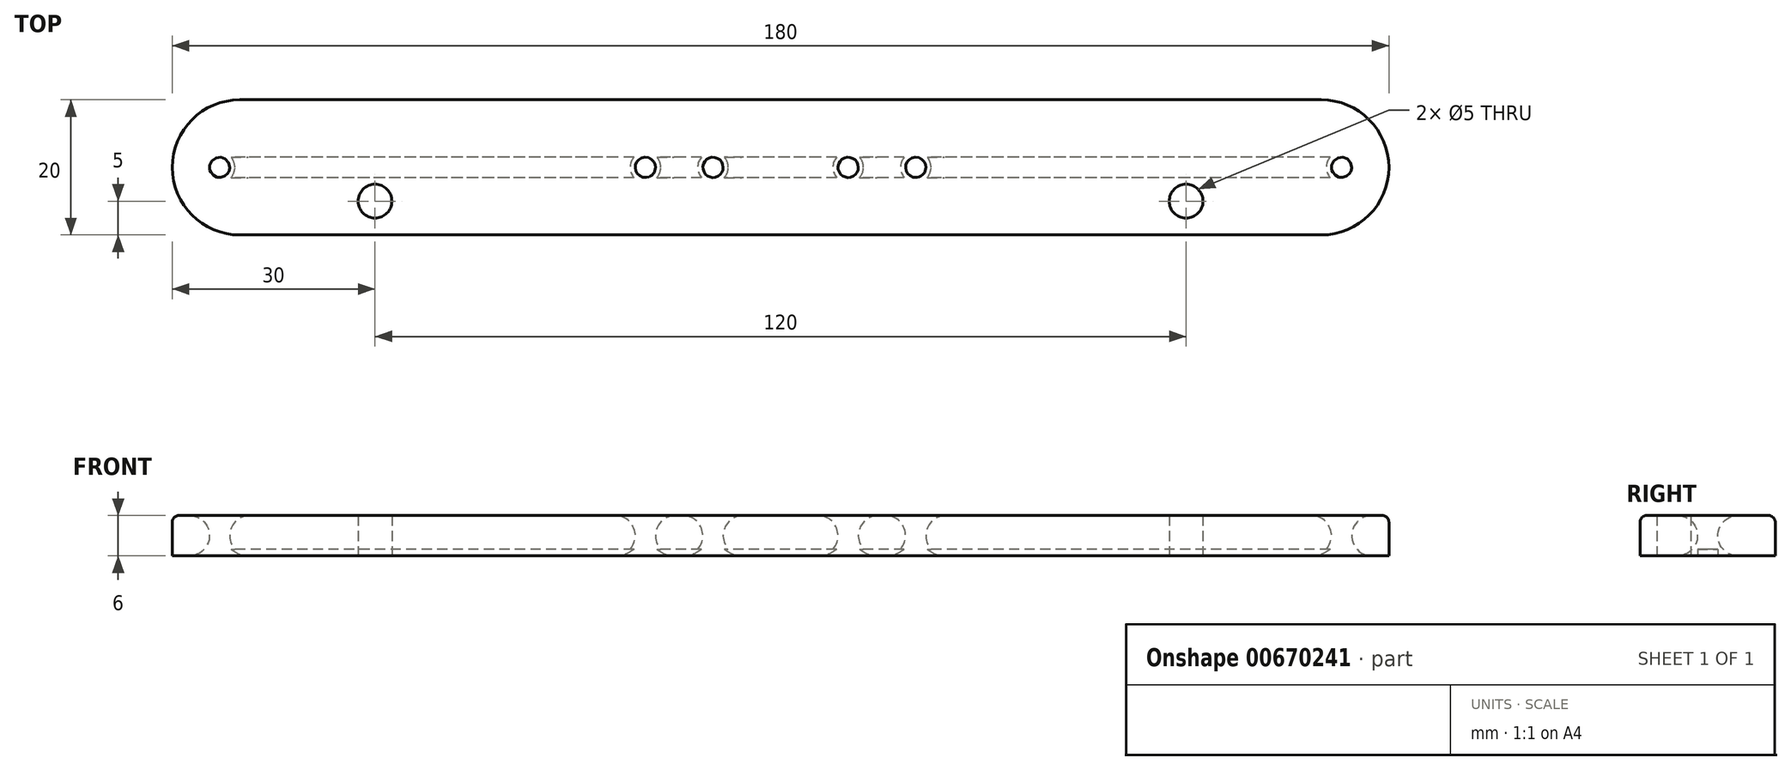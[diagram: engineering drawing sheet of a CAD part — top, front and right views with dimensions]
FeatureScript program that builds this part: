
annotation { "Feature Type Name" : "Feature", "Feature Type Description" : "" }
export const myFeature = defineFeature(function(context is Context, id is Id, definition is map)
    precondition{}
    {
        {
            var Q0;
            Q0=qCreatedBy(makeId("Top.planeOp"),FACE);
            var sketch = newSketch(context, id + "F0", { "sketchPlane" : qUnion([Q0])});
            skLineSegment(sketch, "E0.bottom", {"start": v(90, 10) * mm, "end": v(-90, 10) * mm});
            skLineSegment(sketch, "E0.top", {"start": v(90, -10) * mm, "end": v(-90, -10) * mm});
            skLineSegment(sketch, "E0.left", {"start": v(90, 10) * mm, "end": v(90, -10) * mm});
            skLineSegment(sketch, "E0.right", {"start": v(-90, 10) * mm, "end": v(-90, -10) * mm});
            skPoint(sketch, "E0.middle", {"position": v(0, 0) * mm});
            skCircle(sketch, "E1", {"center": v(-83, 0) * mm, "radius": 1.5 * mm});
            skCircle(sketch, "E2", {"center": v(-10, 0) * mm, "radius": 1.5 * mm});
            skCircle(sketch, "E3", {"center": v(-20, 0) * mm, "radius": 1.5 * mm});
            skCircle(sketch, "E4", {"center": v(10, 0) * mm, "radius": 1.5 * mm});
            skCircle(sketch, "E5", {"center": v(20, 0) * mm, "radius": 1.5 * mm});
            skCircle(sketch, "E6", {"center": v(83, 0) * mm, "radius": 1.5 * mm});
            skSolve(sketch);
        }
        {
            var Q0;
            Q0=makeQuery(id+"F0.imprint","IMPRINT",FACE,{"disambiguationData":[TD([[makeQuery(id+"F0.imprint","IMPRINT",EDGE,{"derivedFrom":sQuery(id+"F0.wireOp",EDGE,"E0.bottom")}),1.0]])]});
            extrude(context, id + "F1", {"entities" : qUnion([Q0]), "depth" : 6 * mm, "offsetDistance" : 25 * mm});
        }
        {
            var Q0;
            Q0=makeQuery(id+"F1.opExtrude","CAP_EDGE",EDGE,{"disambiguationData":[OSD([sQuery(id+"F0.wireOp",EDGE,"E1")])],"isStart":false});
            var Q1;
            Q1=makeQuery(id+"F1.opExtrude","CAP_EDGE",EDGE,{"disambiguationData":[OSD([sQuery(id+"F0.wireOp",EDGE,"E6")])],"isStart":false});
            var Q2;
            Q2=makeQuery(id+"F1.opExtrude","CAP_EDGE",EDGE,{"disambiguationData":[OSD([sQuery(id+"F0.wireOp",EDGE,"E1")])],"isStart":true});
            var Q3;
            Q3=makeQuery(id+"F1.opExtrude","CAP_EDGE",EDGE,{"disambiguationData":[OSD([sQuery(id+"F0.wireOp",EDGE,"E6")])],"isStart":true});
            var Q4;
            Q4=makeQuery(id+"F1.opExtrude","CAP_EDGE",EDGE,{"disambiguationData":[OSD([sQuery(id+"F0.wireOp",EDGE,"E5")])],"isStart":true});
            var Q5;
            Q5=makeQuery(id+"F1.opExtrude","CAP_EDGE",EDGE,{"disambiguationData":[OSD([sQuery(id+"F0.wireOp",EDGE,"E4")])],"isStart":true});
            var Q6;
            Q6=makeQuery(id+"F1.opExtrude","CAP_EDGE",EDGE,{"disambiguationData":[OSD([sQuery(id+"F0.wireOp",EDGE,"E2")])],"isStart":true});
            var Q7;
            Q7=makeQuery(id+"F1.opExtrude","CAP_EDGE",EDGE,{"disambiguationData":[OSD([sQuery(id+"F0.wireOp",EDGE,"E3")])],"isStart":true});
            var Q8;
            Q8=makeQuery(id+"F1.opExtrude","CAP_EDGE",EDGE,{"disambiguationData":[OSD([sQuery(id+"F0.wireOp",EDGE,"E3")])],"isStart":false});
            var Q9;
            Q9=makeQuery(id+"F1.opExtrude","CAP_EDGE",EDGE,{"disambiguationData":[OSD([sQuery(id+"F0.wireOp",EDGE,"E2")])],"isStart":false});
            var Q10;
            Q10=makeQuery(id+"F1.opExtrude","CAP_EDGE",EDGE,{"disambiguationData":[OSD([sQuery(id+"F0.wireOp",EDGE,"E4")])],"isStart":false});
            var Q11;
            Q11=makeQuery(id+"F1.opExtrude","CAP_EDGE",EDGE,{"disambiguationData":[OSD([sQuery(id+"F0.wireOp",EDGE,"E5")])],"isStart":false});
            fillet(context, id + "F2", {"entities" : qUnion([Q0, Q1, Q2, Q3, Q4, Q5, Q6, Q7, Q8, Q9, Q10, Q11]), "radius" : 3 * mm, "tangentPropagation" : true, "allowEdgeOverflow" : false});
        }
        {
            var Q0;
            Q0=makeQuery(id+"F1.opExtrude","SWEPT_EDGE",EDGE,{"disambiguationData":[OSD([sQuery(id+"F0.wireOp",EDGE,"E0.top"),sQuery(id+"F0.wireOp",EDGE,"E0.right")])]});
            var Q1;
            Q1=makeQuery(id+"F1.opExtrude","SWEPT_EDGE",EDGE,{"disambiguationData":[OSD([sQuery(id+"F0.wireOp",EDGE,"E0.bottom"),sQuery(id+"F0.wireOp",EDGE,"E0.right")])]});
            var Q2;
            Q2=makeQuery(id+"F1.opExtrude","SWEPT_EDGE",EDGE,{"disambiguationData":[OSD([sQuery(id+"F0.wireOp",EDGE,"E0.top"),sQuery(id+"F0.wireOp",EDGE,"E0.left")])]});
            var Q3;
            Q3=makeQuery(id+"F1.opExtrude","SWEPT_EDGE",EDGE,{"disambiguationData":[OSD([sQuery(id+"F0.wireOp",EDGE,"E0.bottom"),sQuery(id+"F0.wireOp",EDGE,"E0.left")])]});
            fillet(context, id + "F3", {"entities" : qUnion([Q0, Q1, Q2, Q3]), "radius" : 10 * mm, "tangentPropagation" : true, "allowEdgeOverflow" : false});
        }
        {
            var Q0;
            Q0=qCreatedBy(makeId("Top.planeOp"),FACE);
            var sketch = newSketch(context, id + "F4", { "sketchPlane" : qUnion([Q0])});
            skLineSegment(sketch, "E7.bottom", {"start": v(83, -1.5) * mm, "end": v(-83, -1.5) * mm});
            skLineSegment(sketch, "E7.top", {"start": v(83, 1.5) * mm, "end": v(-83, 1.5) * mm});
            skLineSegment(sketch, "E7.left", {"start": v(83, -1.5) * mm, "end": v(83, 1.5) * mm});
            skLineSegment(sketch, "E7.right", {"start": v(-83, -1.5) * mm, "end": v(-83, 1.5) * mm});
            skPoint(sketch, "E7.middle", {"position": v(0, 0) * mm});
            skSolve(sketch);
        }
        {
            var Q0;
            Q0=makeQuery(id+"F4.imprint","IMPRINT",FACE,{"disambiguationData":[TD([[makeQuery(id+"F4.imprint","IMPRINT",EDGE,{"derivedFrom":sQuery(id+"F4.wireOp",EDGE,"E7.bottom")}),-1.0]])]});
            extrude(context, id + "F5", {"entities" : qUnion([Q0]), "operationType" : NewBodyOperationType.REMOVE, "depth" : 1 * mm, "offsetDistance" : 25 * mm});
        }
        {
            var Q0;
            Q0=makeQuery(id+"F1.opExtrude","CAP_EDGE",EDGE,{"disambiguationData":[OSD([sQuery(id+"F0.wireOp",EDGE,"E0.top")])],"isStart":false});
            fillet(context, id + "F6", {"entities" : qUnion([Q0]), "radius" : 1 * mm, "tangentPropagation" : true, "allowEdgeOverflow" : false});
        }
        {
            var Q0;
            Q0=qCreatedBy(makeId("Top.planeOp"),FACE);
            var sketch = newSketch(context, id + "F7", { "sketchPlane" : qUnion([Q0])});
            skCircle(sketch, "E8", {"center": v(-60, -5) * mm, "radius": 2.5 * mm});
            skCircle(sketch, "E9", {"center": v(60, -5) * mm, "radius": 2.5 * mm});
            skSolve(sketch);
        }
        {
            var Q0;
            Q0 = qSketchRegion(id + "F7", true);
            extrude(context, id + "F8", {"entities" : qUnion([Q0]), "operationType" : NewBodyOperationType.REMOVE, "depth" : 25 * mm, "offsetDistance" : 25 * mm});
        }
    });
